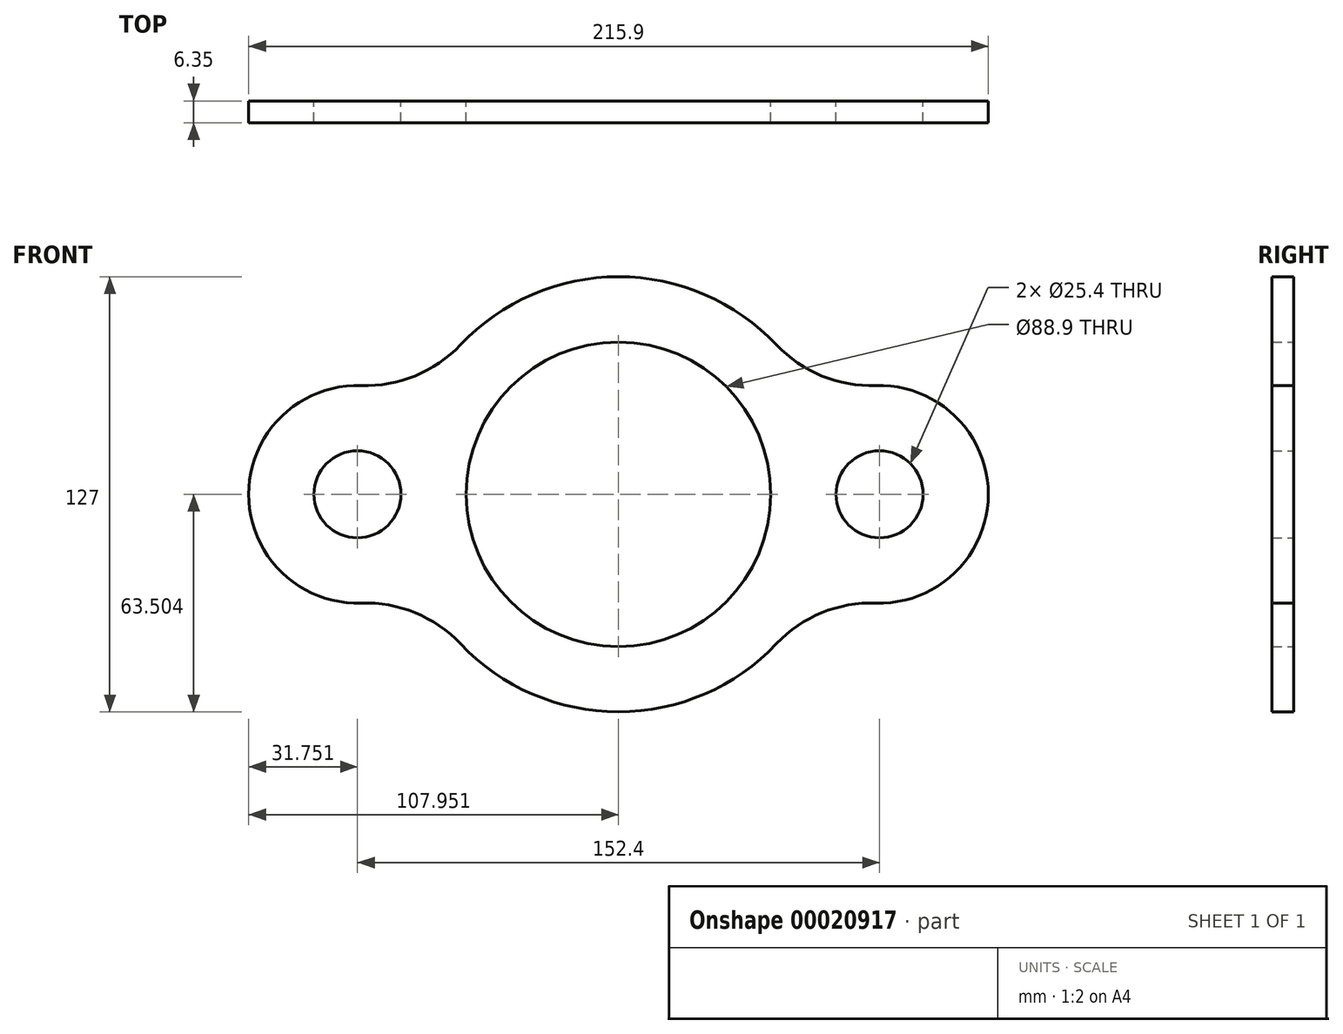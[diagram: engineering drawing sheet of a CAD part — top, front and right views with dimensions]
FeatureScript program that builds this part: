
annotation { "Feature Type Name" : "Feature", "Feature Type Description" : "" }
export const myFeature = defineFeature(function(context is Context, id is Id, definition is map)
    precondition{}
    {
        {
            var Q0;
            Q0=qCreatedBy(makeId("Front.planeOp"),FACE);
            var sketch = newSketch(context, id + "F0", { "sketchPlane" : qUnion([Q0])});
            skCircle(sketch, "E0", {"center": v(-19.74, 8.74) * mm, "radius": 44.45 * mm});
            skCircle(sketch, "E1", {"center": v(-95.94, 8.74) * mm, "radius": 12.7 * mm});
            skCircle(sketch, "E2", {"center": v(56.46, 8.74) * mm, "radius": 12.7 * mm});
            skArc(sketch, "E3", {"start": v(-65.88, -34.89) * mm, "mid": v(-19.74, -54.76) * mm, "end": v(26.4, -34.89) * mm});
            skArc(sketch, "E4", {"start": v(-94.86, 40.48) * mm, "mid": v(-127.69, 8.74) * mm, "end": v(-94.86, -22.99) * mm});
            skArc(sketch, "E5", {"start": v(55.38, -22.99) * mm, "mid": v(88.21, 8.74) * mm, "end": v(55.38, 40.48) * mm});
            skArc(sketch, "E6", {"start": v(-94.86, 40.48) * mm, "mid": v(-79.09, 43.3) * mm, "end": v(-65.88, 52.37) * mm});
            skArc(sketch, "E7", {"start": v(26.4, 52.37) * mm, "mid": v(39.6, 43.3) * mm, "end": v(55.38, 40.48) * mm});
            skArc(sketch, "E8", {"start": v(55.38, -22.99) * mm, "mid": v(39.6, -25.82) * mm, "end": v(26.4, -34.89) * mm});
            skArc(sketch, "E9", {"start": v(-65.88, -34.89) * mm, "mid": v(-79.09, -25.82) * mm, "end": v(-94.86, -22.99) * mm});
            skArc(sketch, "E10.trimOffspring", {"start": v(26.4, 52.37) * mm, "mid": v(-19.74, 72.24) * mm, "end": v(-65.88, 52.37) * mm});
            skSolve(sketch);
        }
        {
            var Q0;
            Q0 = qSketchRegion(id + "F0", true);
            extrude(context, id + "F1", {"entities" : qUnion([Q0]), "depth" : 6.35 * mm});
        }
    });
